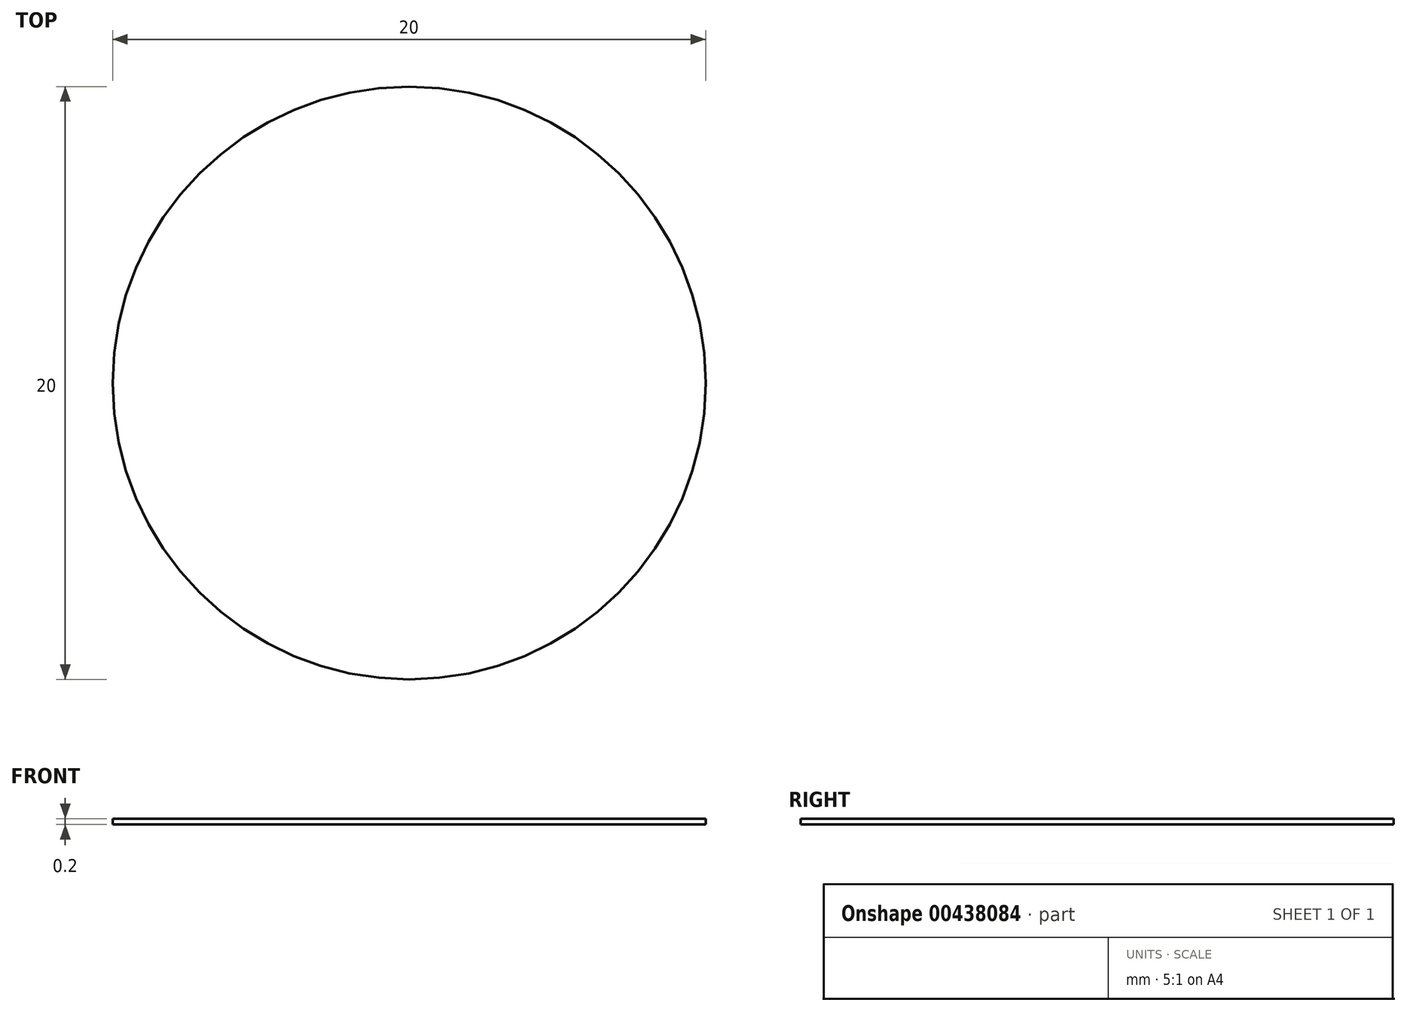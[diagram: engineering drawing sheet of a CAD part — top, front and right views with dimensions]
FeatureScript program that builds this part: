
annotation { "Feature Type Name" : "Feature", "Feature Type Description" : "" }
export const myFeature = defineFeature(function(context is Context, id is Id, definition is map)
    precondition{}
    {
        {
            var Q0;
            Q0=qCreatedBy(makeId("Top.planeOp"),FACE);
            var sketch = newSketch(context, id + "F0", { "sketchPlane" : qUnion([Q0])});
            skCircle(sketch, "E0", {"center": v(0, 0) * mm, "radius": 10 * mm});
            skSolve(sketch);
        }
        {
            var Q0;
            Q0=qSketchRegion(id+"F0",true);
            extrude(context, id + "F1", {"entities" : qUnion([Q0]), "depth" : 0.2 * mm});
        }
    });
